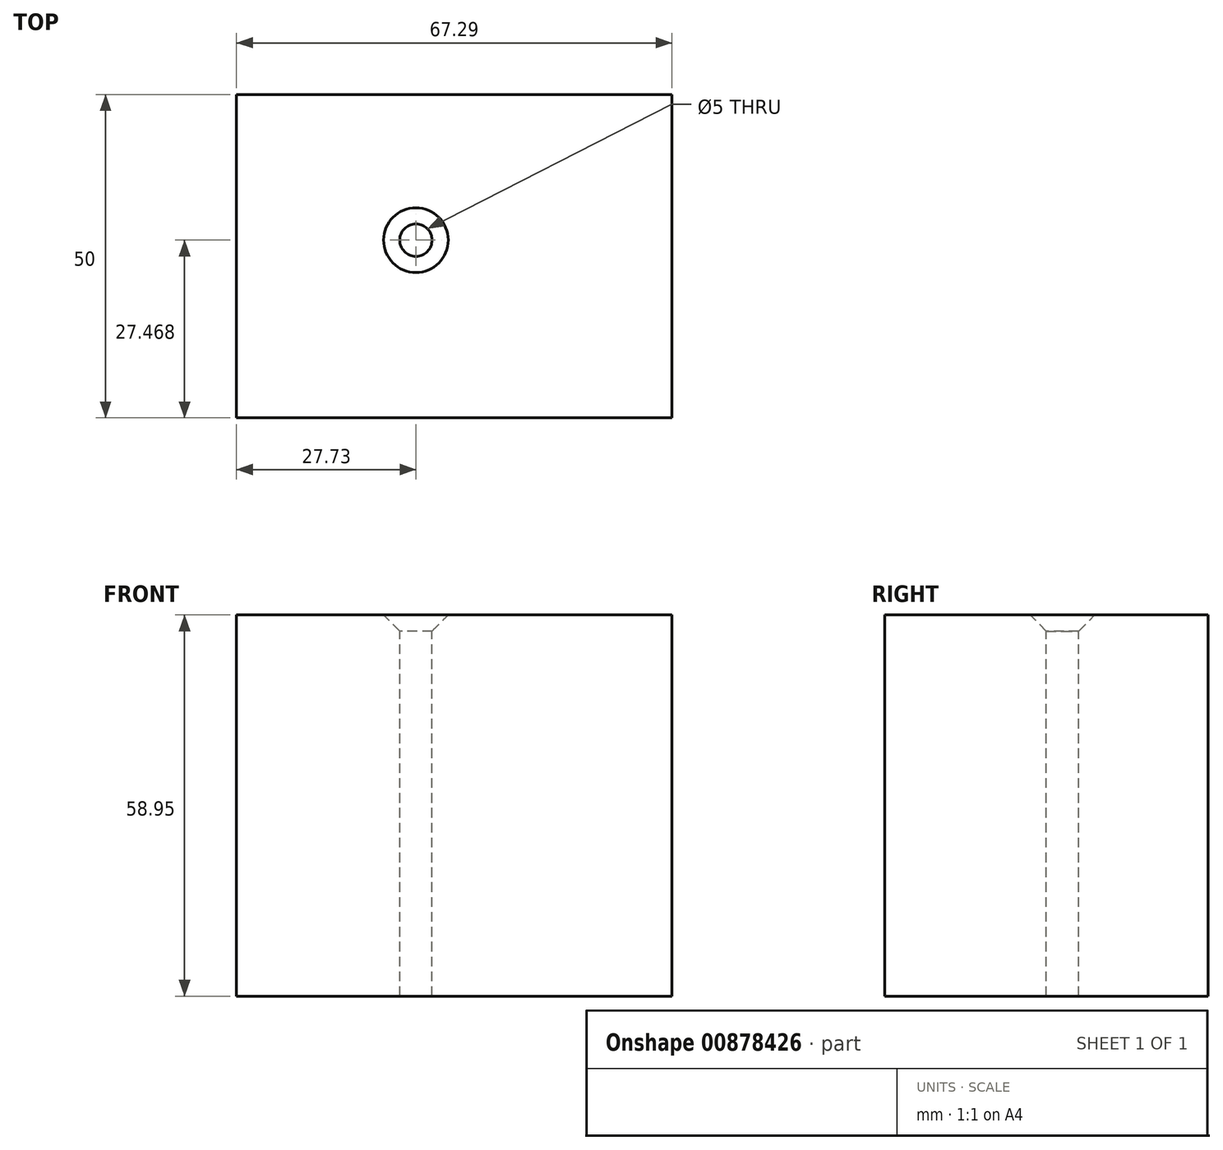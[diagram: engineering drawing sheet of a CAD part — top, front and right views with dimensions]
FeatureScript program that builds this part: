
annotation { "Feature Type Name" : "Feature", "Feature Type Description" : "" }
export const myFeature = defineFeature(function(context is Context, id is Id, definition is map)
    precondition{}
    {
        {
            var Q0;
            Q0=qCreatedBy(makeId("Front.planeOp"),FACE);
            var sketch = newSketch(context, id + "F0", { "sketchPlane" : qUnion([Q0])});
            skLineSegment(sketch, "E0.bottom", {"start": v(-27.73, 31.18) * mm, "end": v(39.56, 31.18) * mm});
            skLineSegment(sketch, "E0.top", {"start": v(-27.73, -27.77) * mm, "end": v(39.56, -27.77) * mm});
            skLineSegment(sketch, "E0.left", {"start": v(-27.73, 31.18) * mm, "end": v(-27.73, -27.77) * mm});
            skLineSegment(sketch, "E0.right", {"start": v(39.56, 31.18) * mm, "end": v(39.56, -27.77) * mm});
            skSolve(sketch);
        }
        {
            var Q0;
            Q0=makeQuery(id+"F0.imprint","IMPRINT",FACE,{"disambiguationData":[TD([[makeQuery(id+"F0.imprint","IMPRINT",EDGE,{"derivedFrom":sQuery(id+"F0.wireOp",EDGE,"E0.bottom")}),-1.0]])]});
            extrude(context, id + "F1", {"entities" : qUnion([Q0]), "depth" : 50 * mm, "offsetDistance" : 25 * mm});
        }
        {
            var Q0;
            Q0=makeQuery(id+"F1.opExtrude","SWEPT_FACE",FACE,{"disambiguationData":[OSD([sQuery(id+"F0.wireOp",EDGE,"E0.bottom")])]});
            var sketch = newSketch(context, id + "F2", { "sketchPlane" : qUnion([Q0])});
            skCircle(sketch, "E1", {"center": v(0, -22.53) * mm, "radius": 6 * mm});
            skSolve(sketch);
        }
        {
            var Q0;
            Q0=sQuery(id+"F2.wireOp",VERTEX,"E1.center");
            var Q1;
            Q1=makeQuery(id+"F1.opExtrude","SWEPT_BODY",BODY,{"disambiguationData":[OSD([sQuery(id+"F0.wireOp",EDGE,"E0.bottom"),sQuery(id+"F0.wireOp",EDGE,"E0.top"),sQuery(id+"F0.wireOp",EDGE,"E0.left"),sQuery(id+"F0.wireOp",EDGE,"E0.right")])]});
            hole(context, id + "F3", {"style" : HoleStyle.C_SINK, "endStyle" : HoleEndStyle.THROUGH, "holeDiameter" : 5 * mm, "cSinkDiameter" : 10 * mm, "cSinkAngle" : 90 * degree, "majorDiameter" : 5 * mm, "isTappedThrough" : true, "tappedDepth" : 12 * mm, "tapClearance" : 3, "startFromSketch" : true, "locations" : qUnion([Q0]), "scope" : qUnion([Q1])});
        }
    });
